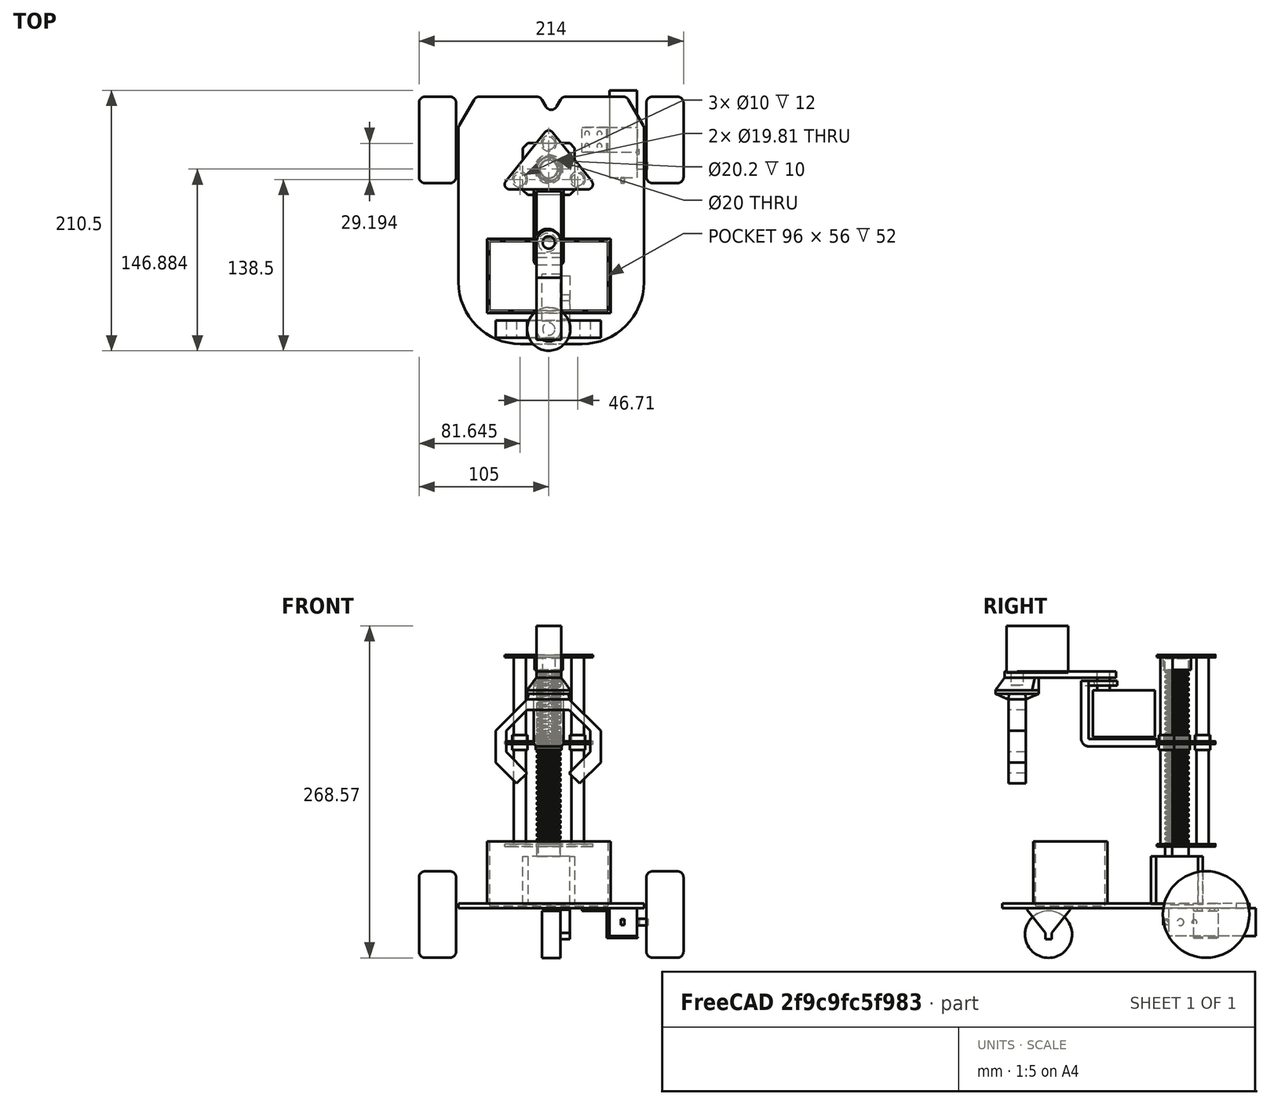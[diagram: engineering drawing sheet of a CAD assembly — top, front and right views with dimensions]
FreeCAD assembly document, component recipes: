
FREECAD ASSEMBLY — COMPONENT RECIPES ("motor_chasis_union")

This assembly document has 3 components, labeled P0..P2 below (a component is one placed body or linked part). 0 of them carry a construction recipe — the FreeCAD feature program that regenerates the part from scratch, quoted from this document or its linked companion documents; the rest are supplied as boundary geometry only. No exploded tour is included for this assembly.
COMPONENT P0 — geometry summary ("Cylinder004"; no construction recipe available for this part):
  bounding box: 10.0 x 4.0 x 4.0 mm
  tessellated surface: 500 triangles
  volume: 126 mm^3 (79% of its bounding box)
  symmetry: 2-fold rotationally symmetric about the x axis; 2-fold rotationally symmetric about the y axis; revolution-symmetric about the z axis through its bounding-box center; mirror-symmetric across its x mid-plane, y mid-plane, z mid-plane
COMPONENT P1 — geometry summary ("Cylinder005"; no construction recipe available for this part):
  bounding box: 10.0 x 4.0 x 4.0 mm
  tessellated surface: 500 triangles
  volume: 126 mm^3 (79% of its bounding box)
  symmetry: 2-fold rotationally symmetric about the x axis; 2-fold rotationally symmetric about the y axis; revolution-symmetric about the z axis through its bounding-box center; mirror-symmetric across its x mid-plane, y mid-plane, z mid-plane
COMPONENT P2 — geometry summary ("Cylinder006"; no construction recipe available for this part):
  bounding box: 10.0 x 4.0 x 4.0 mm
  tessellated surface: 500 triangles
  volume: 126 mm^3 (79% of its bounding box)
  symmetry: 2-fold rotationally symmetric about the x axis; 2-fold rotationally symmetric about the y axis; revolution-symmetric about the z axis through its bounding-box center; mirror-symmetric across its x mid-plane, y mid-plane, z mid-plane
PROVENANCE & LICENSES
A FreeCAD (.FCStd) document from a public repository crawl; recipes are the document's own serialized feature recipes (and, for linked parts, companion documents' recipes).
License: lgpl-2.1.
